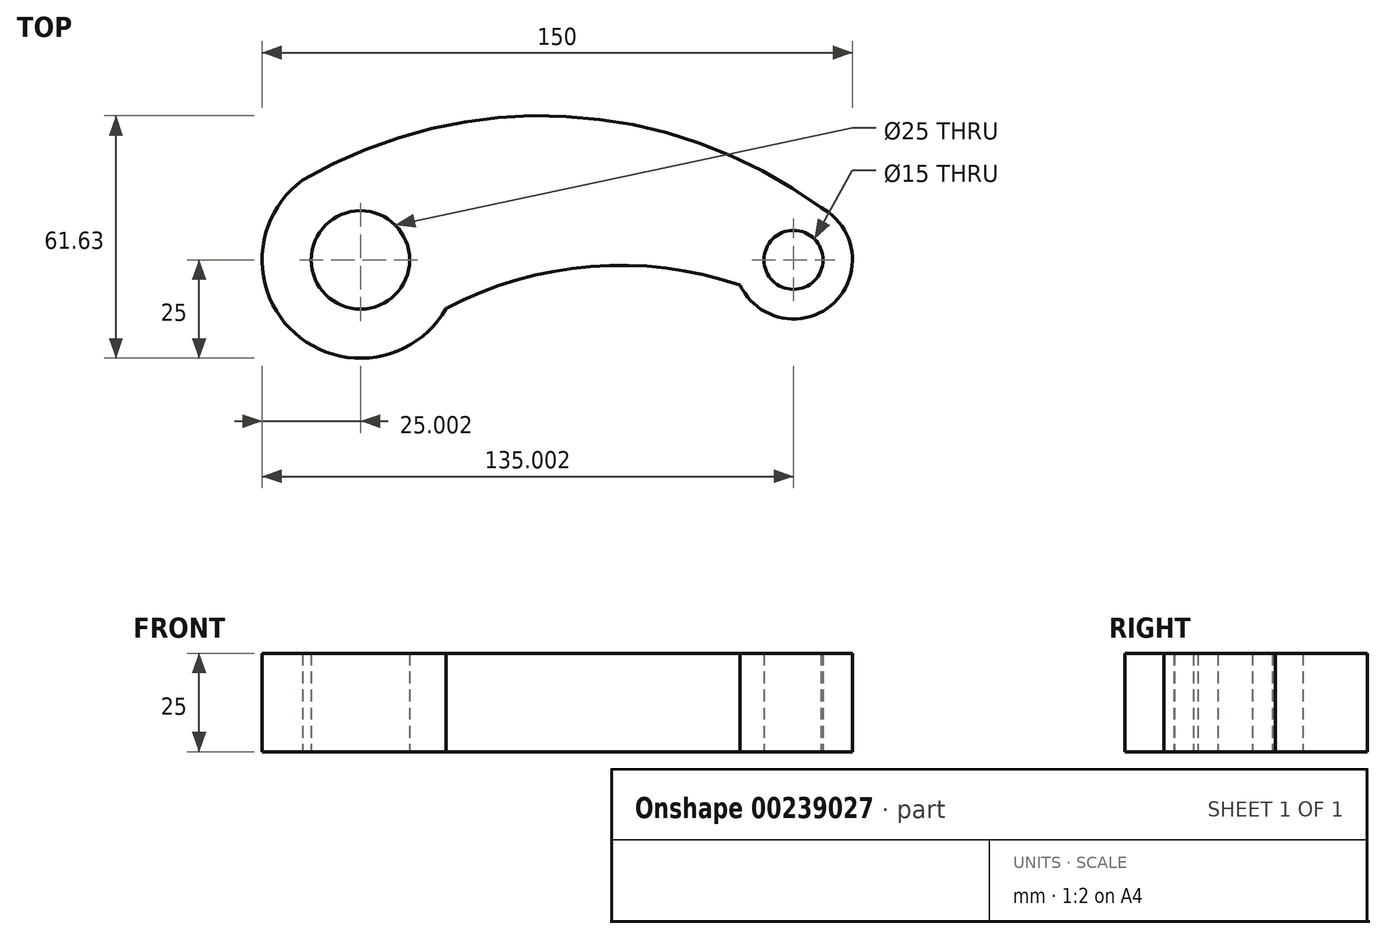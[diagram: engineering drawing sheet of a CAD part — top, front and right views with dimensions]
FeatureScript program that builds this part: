
annotation { "Feature Type Name" : "Feature", "Feature Type Description" : "" }
export const myFeature = defineFeature(function(context is Context, id is Id, definition is map)
    precondition{}
    {
        {
            var Q0;
            Q0=qCreatedBy(makeId("Top.planeOp"),FACE);
            var sketch = newSketch(context, id + "F0", { "sketchPlane" : qUnion([Q0])});
            skCircle(sketch, "E0", {"center": v(-56.13, 48.09) * mm, "radius": 12.5 * mm});
            skArc(sketch, "E1", {"start": v(-65.36, 71.32) * mm, "mid": v(-74.98, 31.68) * mm, "end": v(-34.39, 35.74) * mm});
            skCircle(sketch, "E2", {"center": v(53.87, 48.09) * mm, "radius": 7.5 * mm});
            skArc(sketch, "E3", {"start": v(40.3, 41.7) * mm, "mid": v(64.24, 37.25) * mm, "end": v(60.86, 61.36) * mm});
            skArc(sketch, "E4", {"start": v(60.86, 61.36) * mm, "mid": v(-3.93, 84.55) * mm, "end": v(-70.8, 68.33) * mm});
            skArc(sketch, "E5", {"start": v(40.3, 41.7) * mm, "mid": v(2.34, 46.4) * mm, "end": v(-34.39, 35.74) * mm});
            skSolve(sketch);
        }
        {
            var Q0;
            Q0=makeQuery(id+"F0.imprint","IMPRINT",FACE,{"disambiguationData":[TD([[makeQuery(id+"F0.imprint","IMPRINT",EDGE,{"derivedFrom":sQuery(id+"F0.wireOp",EDGE,"E0")}),-1.0]])]});
            extrude(context, id + "F1", {"entities" : qUnion([Q0]), "depth" : 25 * mm});
        }
    });
